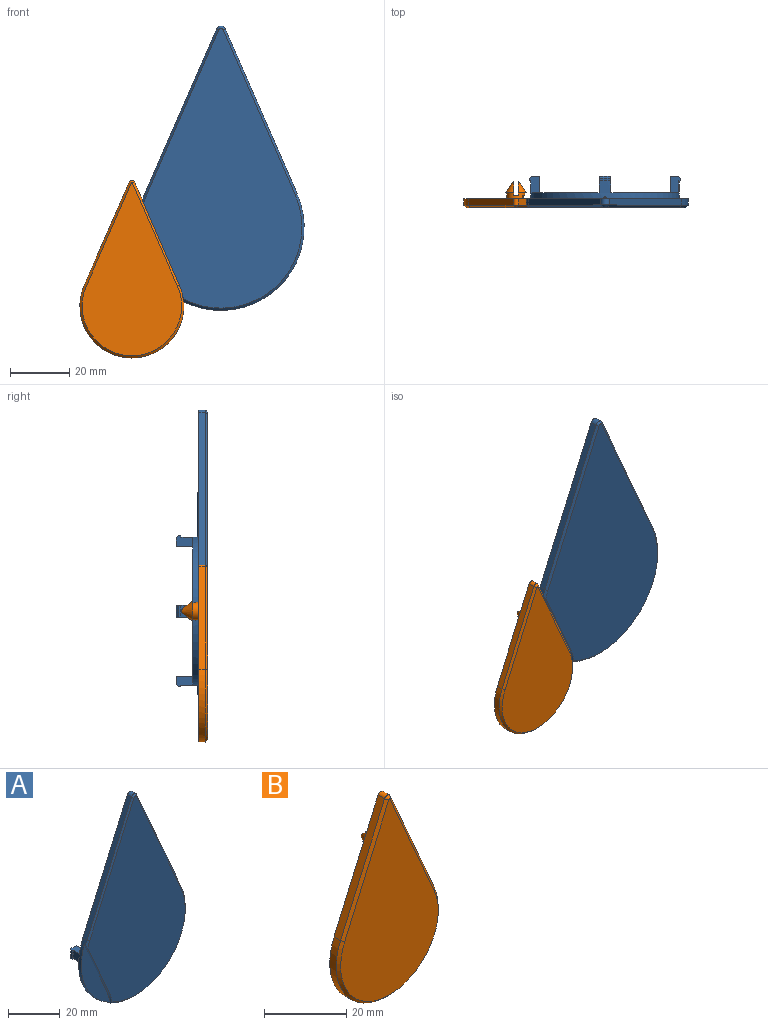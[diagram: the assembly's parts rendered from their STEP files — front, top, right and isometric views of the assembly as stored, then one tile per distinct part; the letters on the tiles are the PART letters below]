
ASSEMBLY  parts=2 mates=1
PART A: 48 faces, bbox 56x10.5x95.8 mm
  f0: cylinder r=0.81mm len=3mm, axis (0,0,-1), area 5.7mm2, adj f4,f5,f11
  f1: plane 94.25x53.27mm, normal (0,-1,0), area 3012mm2, adj f2,f40,f41,f42,f43,f46,f47
  f2: cone r=27.25mm half-angle=45deg, axis (0,1,0), area 2.8mm2, adj f1,f11,f42,f47
  f3: plane 1.5x0.5mm, normal (0,0,1), area 0.5mm2, adj f5,f44
  f4: cylinder r=25mm len=50mm, axis (0,-1,0), area 377.1mm2, adj f0,f5,f6,f7,f8,f9,f14,f15
  f5: plane 95.74x56mm, normal (0,1,0), area 1357.5mm2, adj f0,f3,f4,f10,f11,f12,f13,f44
  f6: plane 22.92x22.92mm, normal (0,1,0), area 98.4mm2, adj f4,f14,f21,f39
  f7: plane 22.92x22.92mm, normal (0,1,0), area 98.4mm2, adj f4,f15,f32,f39
  f8: plane 22.92x22.92mm, normal (0,1,0), area 98.4mm2, adj f4,f26,f33,f39
  f9: plane 22.92x22.92mm, normal (0,1,0), area 98.4mm2, adj f4,f20,f27,f39
  f10: plane 55.65x24.29mm, normal (-0.92,0,0.4), area 136.6mm2, adj f5,f11,f13,f42
  f11: cylinder r=28mm len=56mm, axis (0,1,0), area 220.1mm2, adj f0,f2,f5,f10,f12,f40,f45,f46
  f12: plane 55.65x24.29mm, normal (0.92,0,0.4), area 136.6mm2, adj f5,f11,f13,f41
  f13: cylinder r=1.5mm len=2.75mm, axis (0,1,0), area 7.8mm2, adj f5,f10,f12,f43
  f14: plane 5.5x3.5mm, normal (0,0,1), area 17mm2, adj f4,f6,f16,f17,f18,f19,f39
  f15: plane 5.5x3.5mm, normal (0,0,-1), area 17mm2, adj f4,f7,f16,f17,f18,f19,f39
  f16: cylinder r=25mm len=4mm, axis (0,-1,0), area 3mm2, adj f14,f15,f18,f19
  f17: plane 4x2.83mm, normal (0,1,0), area 11mm2, adj f14,f15,f19,f39
  f18: plane 4x0.58mm, normal (0,-1,0), area 2mm2, adj f4,f14,f15,f16
  f19: cone r=24.25mm half-angle=45deg, axis (0,-1,0), area 4.2mm2, adj f14,f15,f16,f17
  f20: plane 5.5x3.5mm, normal (-1,0,0), area 17mm2, adj f4,f9,f22,f23,f24,f25,f39
  f21: plane 5.5x3.5mm, normal (1,0,0), area 17mm2, adj f4,f6,f22,f23,f24,f25,f39
  f22: cylinder r=25mm len=4mm, axis (0,-1,0), area 3mm2, adj f20,f21,f24,f25
  f23: plane 4x2.83mm, normal (0,1,0), area 11mm2, adj f20,f21,f25,f39
  f24: plane 4x0.58mm, normal (0,-1,0), area 2mm2, adj f4,f20,f21,f22
  f25: cone r=24.25mm half-angle=45deg, axis (0,-1,0), area 4.2mm2, adj f20,f21,f22,f23
  f26: plane 5.5x3.5mm, normal (0,0,-1), area 17mm2, adj f4,f8,f28,f29,f30,f31,f39
  f27: plane 5.5x3.5mm, normal (0,0,1), area 17mm2, adj f4,f9,f28,f29,f30,f31,f39
  f28: cylinder r=25mm len=4mm, axis (0,-1,0), area 3mm2, adj f26,f27,f30,f31
  f29: plane 4x2.83mm, normal (0,1,0), area 11mm2, adj f26,f27,f31,f39
  f30: plane 4x0.58mm, normal (0,-1,0), area 2mm2, adj f4,f26,f27,f28
  f31: cone r=24.25mm half-angle=45deg, axis (0,-1,0), area 4.2mm2, adj f26,f27,f28,f29
  f32: plane 5.5x3.5mm, normal (1,0,0), area 17mm2, adj f4,f7,f34,f35,f36,f37,f39
  f33: plane 5.5x3.5mm, normal (-1,0,0), area 17mm2, adj f4,f8,f34,f35,f36,f37,f39
  f34: cylinder r=25mm len=4mm, axis (0,-1,0), area 3mm2, adj f32,f33,f36,f37
  f35: plane 4x2.83mm, normal (0,1,0), area 11mm2, adj f32,f33,f37,f39
  f36: plane 4x0.58mm, normal (0,-1,0), area 2mm2, adj f4,f32,f33,f34
  f37: cone r=24.25mm half-angle=45deg, axis (0,-1,0), area 4.2mm2, adj f32,f33,f34,f35
  f38: plane 44.02x44.02mm, normal (0,1,0), area 1522mm2, adj f39
  f39: cylinder r=22.01mm len=44.02mm, axis (0,1,0), area 364.7mm2, adj f6,f7,f8,f9,f14,f15,f17,f20
  f40: cone r=27.25mm half-angle=45deg, axis (0,1,0), area 72mm2, adj f1,f11,f41,f46
  f41: plane 55.95x24.98mm, normal (0.65,-0.71,0.28), area 64.4mm2, adj f1,f12,f40,f43
  f42: plane 55.95x24.98mm, normal (-0.65,-0.71,0.28), area 64.4mm2, adj f1,f2,f10,f43
  f43: cone r=0.75mm half-angle=45deg, axis (0,1,0), area 2.8mm2, adj f1,f13,f41,f42
  f44: cylinder r=0.81mm len=15mm, axis (0,0,1), area 28.7mm2, adj f3,f4,f5
  f45: plane 34.15x15.43mm, normal (0,-1,0), area 190.1mm2, adj f11,f46,f47
  f46: cylinder r=17.5mm len=5.48mm, axis (0,-1,0), area 8.2mm2, adj f1,f11,f40,f45,f47
  f47: plane 28.68x12.53mm, normal (-0.92,0,-0.4), area 46.5mm2, adj f1,f2,f11,f45,f46
PART B: 21 faces, bbox 35x8.9x59.8 mm
  f0: plane 6.84x2.75mm, normal (0,-1,0), area 4.3mm2, adj f1,f14,f20
  f1: cone r=0mm half-angle=35deg, axis (0,-1,0), area 24.5mm2, adj f0,f20
  f2: plane 34.65x15.12mm, normal (0.92,0,0.4), area 38.2mm2, adj f3,f5,f6,f9,f12,f13
  f3: plane 59.75x35mm, normal (0,1,0), area 1092.2mm2, adj f2,f4,f5,f6,f12,f14
  f4: plane 34.65x15.12mm, normal (-0.92,0,0.4), area 85.1mm2, adj f3,f5,f6,f10
  f5: cylinder r=17.5mm len=35mm, axis (0,1,0), area 147.6mm2, adj f2,f3,f4,f8,f12,f13
  f6: cylinder r=1mm len=2.25mm, axis (0,1,0), area 5.2mm2, adj f2,f3,f4,f11
  f7: plane 58.25x33.5mm, normal (0,-1,0), area 1198.9mm2, adj f8,f9,f10,f11
  f8: cone r=16.75mm half-angle=45deg, axis (0,1,0), area 72mm2, adj f5,f7,f9,f10
  f9: plane 34.95x15.81mm, normal (0.65,-0.71,0.28), area 40.1mm2, adj f2,f7,f8,f11
  f10: plane 34.95x15.81mm, normal (-0.65,-0.71,0.28), area 40.1mm2, adj f4,f7,f8,f11
  f11: cone r=0.25mm half-angle=45deg, axis (0,1,0), area 1.5mm2, adj f6,f7,f9,f10
  f12: cylinder r=28mm len=34.15mm, axis (0,1,0), area 62.5mm2, adj f2,f3,f5,f13,f14,f15
  f13: plane 34.15x15.43mm, normal (0,1,0), area 190.1mm2, adj f2,f5,f12
  f14: cylinder r=3mm len=6mm, axis (0,-1,0), area 29.8mm2, adj f0,f3,f12,f15,f16,f18,f19,f20
  f15: cone r=3mm half-angle=45deg, axis (0,1,0), area 4.2mm2, adj f12,f14
  f16: plane 6.84x2.75mm, normal (0,-1,0), area 4.3mm2, adj f14,f17,f19
  f17: cone r=0mm half-angle=35deg, axis (0,-1,0), area 24.5mm2, adj f16,f19
  f18: plane 6x1.5mm, normal (0,1,0), area 8.9mm2, adj f14,f19,f20
  f19: plane 6.84x4.93mm, normal (1,0,0), area 21.1mm2, adj f14,f16,f17,f18
  f20: plane 6.84x4.93mm, normal (-1,0,0), area 21.1mm2, adj f0,f1,f14,f18
PLACE A at identity
PLACE B t=(-30,0,-26.54)mm
MATE planar B.f3 <-> A.f5  axis (0,1,0) through (-30,0,-6.54)mm
